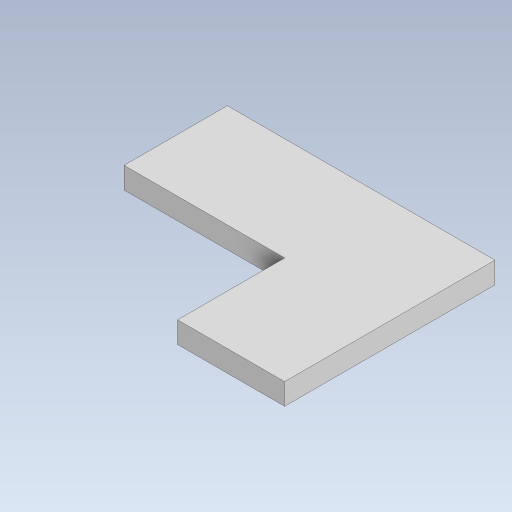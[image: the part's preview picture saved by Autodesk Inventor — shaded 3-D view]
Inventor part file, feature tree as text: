
AUTODESK INVENTOR PART (.ipt)
format: ipt  version: 2023.5 (Build 275446000, 446)  size: 221,696 bytes
history: native  units: in
note: dims shown in document units (in); Inventor stores cm internally (conversion verified against a paired STEP export)
features: extrude x1, sketch x1
ambient origin geometry x8: Origin, YZ Plane, XZ Plane, XY Plane, X Axis, Y Axis, Z Axis, Center Point
bodies: Solid1 (feature_tree)
feature tree (2):
  extrude  "Extrusion1"  Depth=1.5472in
  sketch  "Sketch1"  dims[d0=1.9685in d1=1.5472in d2=1.1811in d3=0.7874in d4=0.1575in d5=0.0in]
